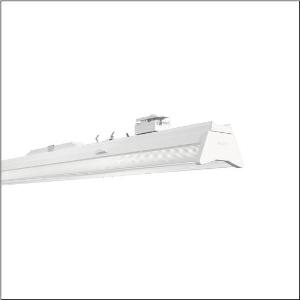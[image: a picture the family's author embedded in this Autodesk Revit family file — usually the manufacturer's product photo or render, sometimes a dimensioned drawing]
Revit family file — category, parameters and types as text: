
# Revit family: licross_r__21_performance_mo_52tm16cn46xg_6fd6
name_source: partatom
category: Lighting Fixtures
units: mm (PartAtom-declared; Revit-internal decimal feet)

## family parameters
Cut with Voids When Loaded = No
Host = Face
Light Source = No
Part Type = Normal
Room Calculation Point = No
Round Connector Dimension = Use Diameter
Shared = No

## types (1)
- --- (1 x LED, 6000 lm, 32 W, 4000K)
    Apparent Load = 32 VA
    CIE Flux Codes = 66 88 96 79 100
    Color Rendering = 80
    Color Temperature = 4000K
    Default Elevation = 1800 mm
    Description = Licross® 21 Performance MO, luminaire insert, of sheet steel, galvanised, coil coated, white, length: 1.500mm, width: 120mm, height: 123mm, LED rated luminous flux: 6.000lm, light colour: 840, control gear: ON/OFF Multilumen, CLOi, control gear: ECG Multilumen, with plug, 3-pole, with phase selection, mains connection: 220..240V, AC, 50/60Hz, start of lifetime: 32W, end of service life: 38W, halogen-free wiring, primary light control with lens, of plastic, primary optical cover: cover, of PMMA, light emission: direct/indirect distribution, primary light characteristic: symmetric, protection rating (complete): IP40, insulation class (complete): insulation class I (protective earthing), certification: CE, ENEC, UKCA, protection symbol: D if used in an environment without relevant dust loads with corresponding accessories, impact resistance: IK06, permissible ambient temperature for indoor applications: -35..+55°C, corresponds to IFS (International Featured Standards) requirements for safety and quality in the food industry, reducing of maximum allowable ambient temperature of 5°C with ceiling mounting, LABS conformity tested according to VDMA 24364:2018-05, packaging unit: 1 piece
    Height = 114 mm
    Lamp = 1 x LED
    Lamp Light Flux = 6000 lm
    Lamp Power = 32 W
    Lamp count = 1
    Length = 1500 mm
    Luminous efficacy = 188 lm/W
    Manufacturer = Siteco
    ModVariant = No
    Model = 52TM16CN46XG
    Mounting Place = Ceiling
    Mounting Type = Pendant
    Number of Poles = 1
    OnlyDefault = Yes
    Power Factor = 1
    Product Name = Licross® 21 Performance MO
    Product group = luminaire insert
    ProductGroupID = 901
    Protection Class = Protection class I
    Protection Degree = IP 40
    RLX_Detail_Level = 1
    RLX_Emergency_Light_Flux = 0 lm
    RLX_Emergency_Type = 0
    RLX_Emergency_Type_DB = No
    RlxData = <blob elided: 31913 chars, md5=393460e0>
    Socket = socket
    Standby Power = 0 W
    System Light Flux = 6000 lm
    System Power = 32 W
    Type Comments = factory setting: luminous flux: 100 % | (A | C | E) | 74 mA
    Type Image = l_1256138.jpg
    URL = http://relux.com
    VarID = @adj_059823
    Voltage = 0 V
    Weight = 0.00 kg
    Width = 120 mm

## geometry (parser evidence)
native form markers: Blend x4, Sweep x13
no freeform markers — native parametric forms only
